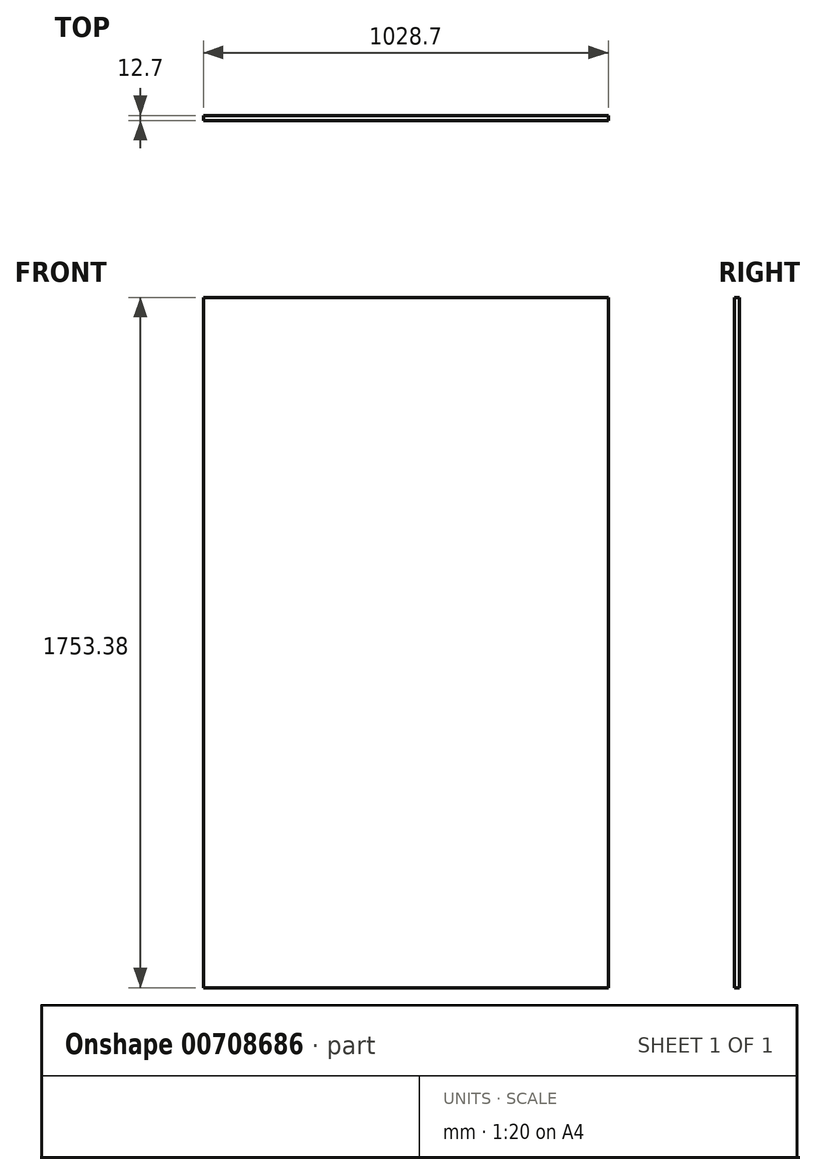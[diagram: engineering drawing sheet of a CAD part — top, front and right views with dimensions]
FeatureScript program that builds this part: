
annotation { "Feature Type Name" : "Feature", "Feature Type Description" : "" }
export const myFeature = defineFeature(function(context is Context, id is Id, definition is map)
    precondition{}
    {
        {
            var Q0;
            Q0=qCreatedBy(makeId("Front.planeOp"),FACE);
            var sketch = newSketch(context, id + "F0", { "sketchPlane" : qUnion([Q0])});
            skLineSegment(sketch, "E0.bottom", {"start": v(514.35, -876.7) * mm, "end": v(-514.35, -876.7) * mm});
            skLineSegment(sketch, "E0.top", {"start": v(514.35, 876.7) * mm, "end": v(-514.35, 876.7) * mm});
            skLineSegment(sketch, "E0.left", {"start": v(514.35, -876.7) * mm, "end": v(514.35, 876.7) * mm});
            skLineSegment(sketch, "E0.right", {"start": v(-514.35, -876.7) * mm, "end": v(-514.35, 876.7) * mm});
            skPoint(sketch, "E0.middle", {"position": v(0, 0) * mm});
            skSolve(sketch);
        }
        {
            var Q0;
            Q0=makeQuery(id+"F0.imprint","IMPRINT",FACE,{"disambiguationData":[TD([[makeQuery(id+"F0.imprint","IMPRINT",EDGE,{"derivedFrom":sQuery(id+"F0.wireOp",EDGE,"E0.bottom")}),-1.0]])]});
            extrude(context, id + "F1", {"entities" : qUnion([Q0]), "depth" : 12.7 * mm, "offsetDistance" : 25.4 * mm});
        }
    });
